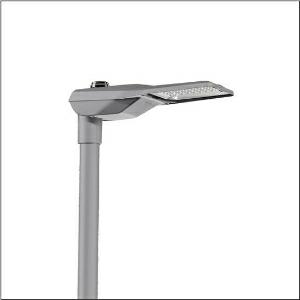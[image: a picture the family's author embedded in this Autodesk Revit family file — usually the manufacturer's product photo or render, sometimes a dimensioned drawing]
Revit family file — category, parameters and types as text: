
# Revit family: streetlight_sl_21_mini___p0_8a_5xe6u47n08gb_070e
name_source: partatom
category: Lighting Fixtures
units: mm (PartAtom-declared; Revit-internal decimal feet)

## family parameters
Cut with Voids When Loaded = No
Host = Face
Light Source = No
Part Type = Normal
Room Calculation Point = No
Round Connector Dimension = Use Diameter
Shared = No

## types (1)
- --- (1 x LED, 6240 lm, 40.4 W, 4000K)
    Apparent Load = 40 VA
    CIE Flux Codes = 33 69 96 100 100
    Color Rendering = 70
    Color Temperature = 4000K
    Default Elevation = 1800 mm
    Description = Streetlight SL 21 mini, mast luminaire, primary light control with lens, of PMMA, primary optical cover: cover, of toughened safety glass, transparent, light distribution: P0.8a, light emission: direct distribution, primary light characteristic: asymmetric, installation type: side-entry, LED, 3G 1.5mm², High Power LED, rated luminous flux: 6.240lm, luminous efficacy: 155lm/W, light colour: 740, colour temperature: 4000K, control gear: NEMA (7pin), control: flexible luminous flux parameterisation, time-dependent luminous flux control, constant luminous flux control, pre-setting: linear dimming characteristic, overheat protection, mains connection: 230..240V, AC, 50/60Hz, connection cable pre-assembled, cable length: 8,5m, wiring characteristics: H07RN-F, start of lifetime: 40W, end of service life: 41W, reduction: 19W, luminaire housing, of diecast aluminium (EN AC-44300), powder-coated, SITECO metallic grey (DB 702S), corrosivity category C5 high according to DIN EN ISO 12944, multi-level sealing system, sealing non-destructively replaceable, inclination adjustable: 0°, 5°, 10°, 15°, length: 628mm, width: 235mm, height: 110mm, spigot size: 42mm (side-entry), mounting height: 4..8m, protection rating (complete): IP66, insulation class (complete): insulation class I (protective earthing), certification: CE, ENEC, ENEC+, VDE, impact resistance: IK10, permissible operating ambient temperature for outdoor applications: -40..+50°C, standard-compliant lighting for roads and squares, packaging unit: 1 piece

Light Distribution: P0.8a
    Height = 110 mm
    Lamp = 1 x LED
    Lamp Light Flux = 6240 lm
    Lamp Power = 40.4 W
    Lamp count = 1
    Length = 625 mm
    Luminous efficacy = 154 lm/W
    Manufacturer = Siteco
    ModVariant = No
    Model = 5XE6U47N08GB
    Number of Poles = 1
    OnlyDefault = Yes
    Power Factor = 1
    Product Name = Streetlight SL 21 mini | P0.8a
    Product group = mast luminaire | pylon top
    ProductGroupID = 6100
    Protection Class = Protection class I
    Protection Degree = IP 66
    RLX_Detail_Level = 1
    RLX_Emergency_Light_Flux = 0 lm
    RLX_Emergency_Type = 0
    RLX_Emergency_Type_DB = No
    RlxData = <blob elided: 91449 chars, md5=66fca226>
    Socket = socket
    Standby Power = 0 W
    System Light Flux = 6240 lm
    System Power = 40 W
    Type Comments = factory setting: luminous flux: 100 % | dim-lin: 254 | 812 mA
    Type Image = l_1294379.jpg
    URL = http://relux.com
    VarID = @adj_081285
    Voltage = 0 V
    Weight = 0.00 kg
    Width = 234 mm

## geometry (parser evidence)
native form markers: Blend x4, Sweep x12
no freeform markers — native parametric forms only
